# Revit family: Fixture_Support_Elongated_EZCarry_Horizontal-Zurn-ZE1201-N_4-FMBO
name_source: partatom
category: Plumbing Fixtures
units: mm (PartAtom-declared; Revit-internal decimal feet)

## family parameters
Always vertical = Yes
Cut with Voids When Loaded = No
Maintain Annotation Orientation = No
OmniClass Number = 23.45.55.11
OmniClass Title = Sanitary Components
Part Type = Normal
Room Calculation Point = No
Round Connector Dimension = Use Radius
Shared = No
Work Plane-Based = No

## types (2) — shared parameters
Approx. Weight (Lbs) = 56.00 lb
Assembly Code = D2030400
CW Connection = No
Connector Radius = 2 "
Coupling Material = ABS - Zurn - Plastic
Coupling Range = 2 "
Default Elevation = 25 "
Description = ELONGATED BARREL FITTING 38 [965] EZCARRY® ADJUSTABLE HORIZONTAL HIGH PERFORMANCE SIPHON JET NO-HUB WATER CLOSET CARRIER SYSTEM W/ FLOOR MOUNT BACK OUTLET FIXTURE SUPPORT
Dimension_N = 8.563 "
HW Connection = No
Half side Length A = 9.125 "
Half side Length_B = 3.125 "
Hardware = Steel - Zurn  - Galvanized
Height = 10.75 "
Horizontal Pipe length = 38 "
Left Connector = Yes
Main Material = Iron - Zurn - Cast - Painted - Blue
Manufacturer = Zurn Water, LLC
Manufacurer Brand = Zurn
Model = ZE1201-N_4-FMBO
Modified Date = 02/6/2026
Pipe Size_A Inside Diameter = 4.026 "
Pipe Size_A Inside Radius = 2.013 "
Pipe Size_A Nominal Diameter = 4 "
Pipe Size_A Outer Diameter = 4.5 "
Pipe Size_A Outer Radius = 2.25 "
Product Documentation Link = https://files.zurn.com
Product Page URL = https://www.zurn.com
Product data url = https://www.bimobject.com
URL = www.zurn.com
Vent Connection = Yes
Vent Radius = 1 "
WFU = 1
Waste Connection = Yes
Water Closet Nominal radius = 1.5 "
Water Closet outer radius = 1.75 "
zero-valued in all types: CWFU, HWFU

## per-type parameters (varying)
| type | Connector | Dimension_K | Z1201-NL4_FMBO | Z1201-NR4_FMBO |
| ZE1201-NR4_FMBO | 2.313 " | 4.126 " | No | Yes |
| ZE1201-NL4_FMBO | 2.375 " | 4.125 " | Yes | No |

## geometry (parser evidence)
native form markers: Blend x8, Sweep x29
no freeform markers — native parametric forms only
